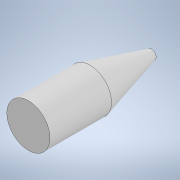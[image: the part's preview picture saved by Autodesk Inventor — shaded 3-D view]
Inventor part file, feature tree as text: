
AUTODESK INVENTOR PART (.ipt)
format: ipt  version: 2021 (Build 250183000, 183)  size: 103,936 bytes
history: native  units: mm
features: sketch x2, extrude x1, plane x1, loft x1, other x1
ambient origin geometry x8: Origin, YZ Plane, XZ Plane, XY Plane, X Axis, Y Axis, Z Axis, Center Point
bodies: Solid1 (feature_tree)
feature tree (6):
  extrude  "Extrusion1"  Depth=10.0mm TaperAngle=0.0deg
  plane  "Work Plane1"
  loft  "Loft1"
  sketch  "Sketch1"  dims[d0=7.0mm d1=10.0mm d2=0.0mm]
  sketch  "Sketch2"  dims[d3=10.0mm d4=1.5mm d5=0.0mm d6=90.0deg d7=0.0mm d8=90.0deg]
  other  "Edges1"
